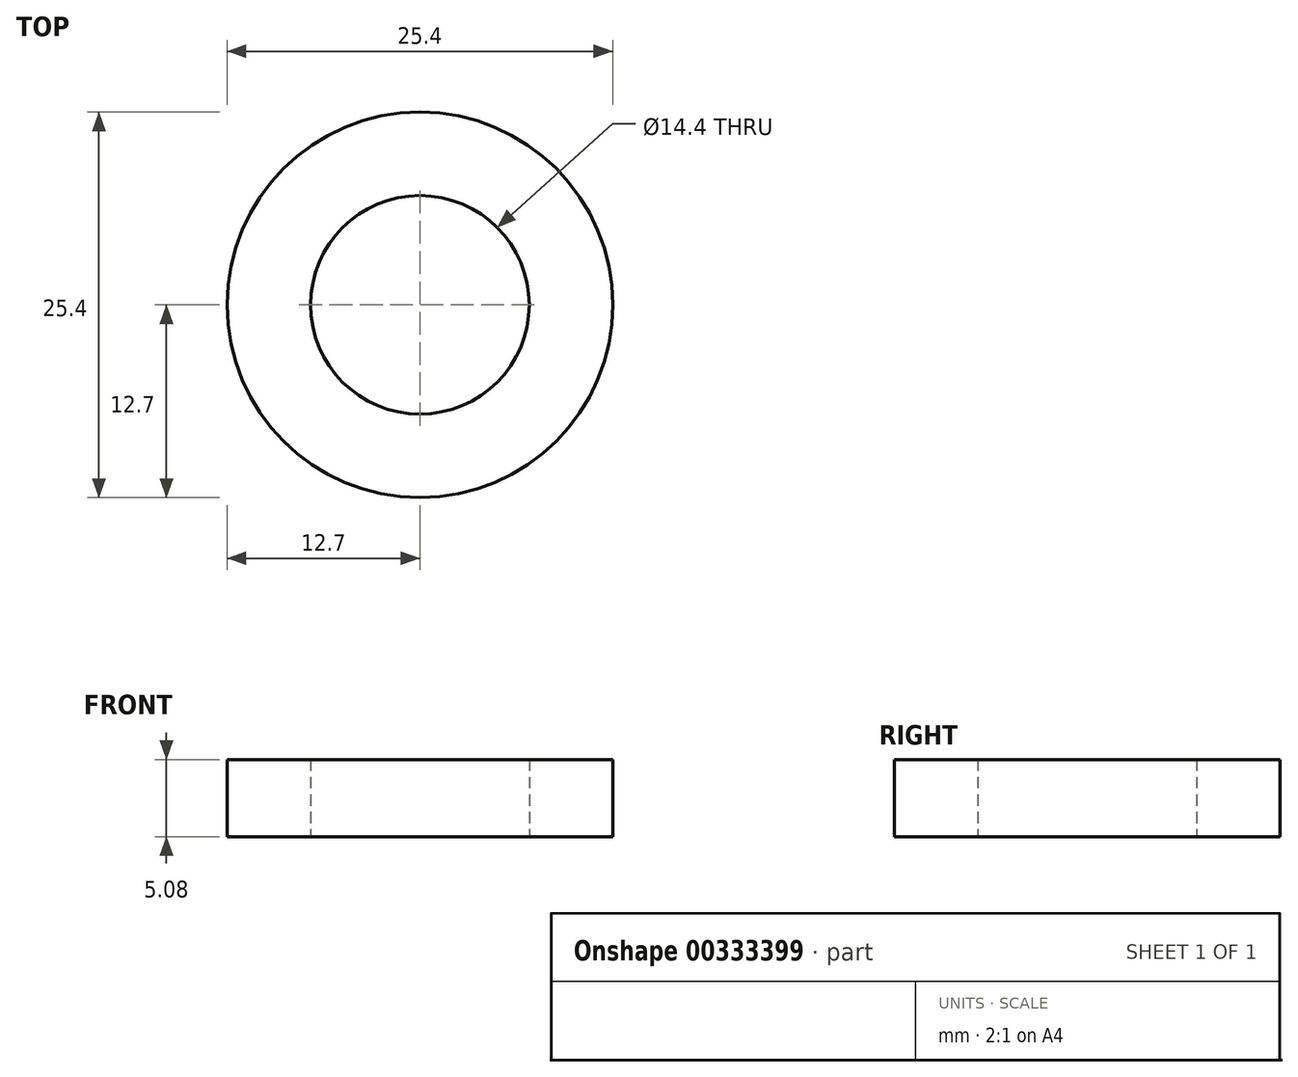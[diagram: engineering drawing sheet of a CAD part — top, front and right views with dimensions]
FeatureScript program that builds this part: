
annotation { "Feature Type Name" : "Feature", "Feature Type Description" : "" }
export const myFeature = defineFeature(function(context is Context, id is Id, definition is map)
    precondition{}
    {
        {
            var Q0;
            Q0=qCreatedBy(makeId("Top.planeOp"),FACE);
            var sketch = newSketch(context, id + "F0", { "sketchPlane" : qUnion([Q0])});
            skCircle(sketch, "E0", {"center": v(0, 0) * mm, "radius": 7.2 * mm});
            skCircle(sketch, "E1", {"center": v(0, 0) * mm, "radius": 12.7 * mm});
            skSolve(sketch);
        }
        {
            var Q0;
            Q0=makeQuery(id+"F0.imprint","IMPRINT",FACE,{"disambiguationData":[TD([[makeQuery(id+"F0.imprint","IMPRINT",EDGE,{"derivedFrom":sQuery(id+"F0.wireOp",EDGE,"E0")}),-1.0]])]});
            extrude(context, id + "F1", {"entities" : qUnion([Q0]), "depth" : 5.08 * mm});
        }
    });
